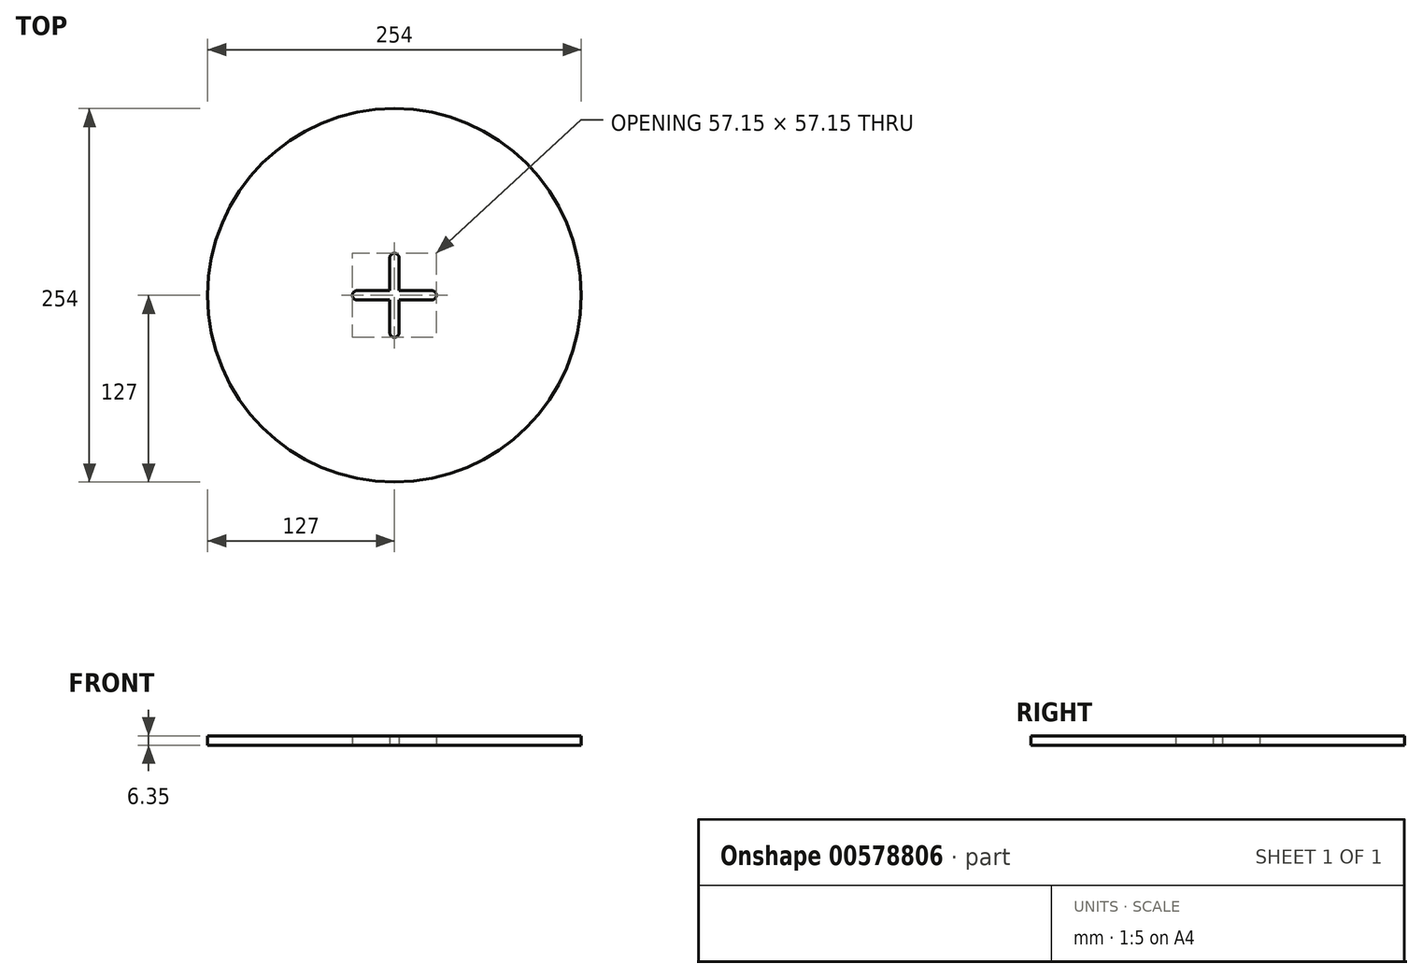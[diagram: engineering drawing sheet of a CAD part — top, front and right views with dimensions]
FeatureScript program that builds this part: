
annotation { "Feature Type Name" : "Feature", "Feature Type Description" : "" }
export const myFeature = defineFeature(function(context is Context, id is Id, definition is map)
    precondition{}
    {
        {
            var Q0;
            Q0=qCreatedBy(makeId("Top.planeOp"),FACE);
            var sketch = newSketch(context, id + "F0", { "sketchPlane" : qUnion([Q0])});
            skCircle(sketch, "E0", {"center": v(0, 0) * mm, "radius": 127 * mm});
            skLineSegment(sketch, "E1", {"start": v(-3.17, -3.17) * mm, "end": v(-25.4, -3.18) * mm});
            skLineSegment(sketch, "E2", {"start": v(-25.4, 3.17) * mm, "end": v(-3.17, 3.18) * mm});
            skArc(sketch, "E3", {"start": v(-25.4, 3.18) * mm, "mid": v(-28.58, 0) * mm, "end": v(-25.4, -3.18) * mm});
            skArc(sketch, "E4.MirrorCS", {"start": v(25.4, 3.18) * mm, "mid": v(28.58, 0) * mm, "end": v(25.4, -3.17) * mm});
            skLineSegment(sketch, "E5.MirrorCS", {"start": v(25.4, 3.18) * mm, "end": v(3.18, 3.18) * mm});
            skLineSegment(sketch, "E6.MirrorCS", {"start": v(3.18, -3.17) * mm, "end": v(25.4, -3.18) * mm});
            skLineSegment(sketch, "E7.left", {"start": v(-3.17, 3.18) * mm, "end": v(-3.17, 25.4) * mm});
            skLineSegment(sketch, "E7.right", {"start": v(3.18, 3.18) * mm, "end": v(3.18, 25.4) * mm});
            skArc(sketch, "E8", {"start": v(3.18, 25.4) * mm, "mid": v(0, 28.58) * mm, "end": v(-3.18, 25.4) * mm});
            skLineSegment(sketch, "E9.MirrorCS", {"start": v(-3.17, -3.17) * mm, "end": v(-3.17, -25.4) * mm});
            skLineSegment(sketch, "E10.MirrorCS", {"start": v(3.18, -3.17) * mm, "end": v(3.18, -25.4) * mm});
            skArc(sketch, "E11.MirrorCS", {"start": v(3.18, -25.4) * mm, "mid": v(0, -28.57) * mm, "end": v(-3.18, -25.4) * mm});
            skSolve(sketch);
        }
        {
            var Q0;
            Q0=makeQuery(id+"F0.imprint","IMPRINT",FACE,{"disambiguationData":[TD([[makeQuery(id+"F0.imprint","IMPRINT",EDGE,{"derivedFrom":sQuery(id+"F0.wireOp",EDGE,"E0")}),1.0]])]});
            extrude(context, id + "F1", {"entities" : qUnion([Q0]), "depth" : 6.35 * mm, "offsetDistance" : 25.4 * mm});
        }
    });
